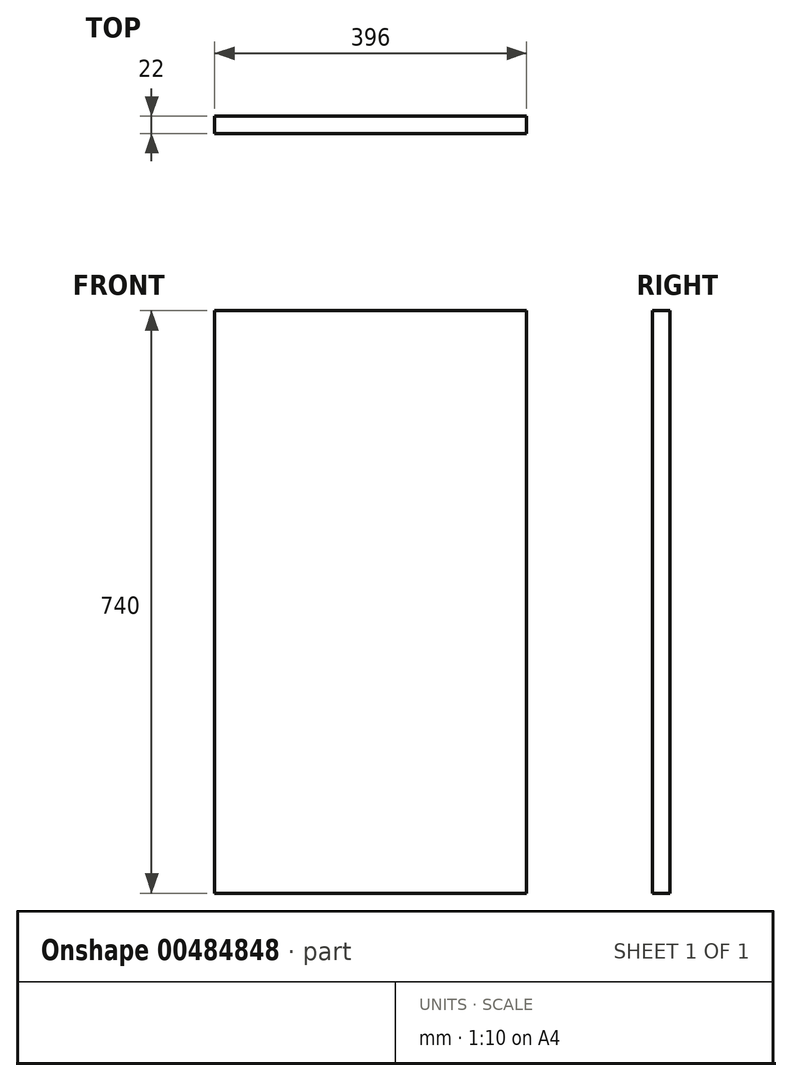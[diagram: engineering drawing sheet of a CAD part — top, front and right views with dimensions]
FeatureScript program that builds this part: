
annotation { "Feature Type Name" : "Feature", "Feature Type Description" : "" }
export const myFeature = defineFeature(function(context is Context, id is Id, definition is map)
    precondition{}
    {
        {
            var Q0;
            Q0=qCreatedBy(makeId("Front.planeOp"),FACE);
            var sketch = newSketch(context, id + "F0", { "sketchPlane" : qUnion([Q0])});
            skLineSegment(sketch, "E0.bottom", {"start": v(-244.74, 172.47) * mm, "end": v(151.26, 172.47) * mm});
            skLineSegment(sketch, "E0.top", {"start": v(-244.74, -567.53) * mm, "end": v(151.26, -567.53) * mm});
            skLineSegment(sketch, "E0.left", {"start": v(-244.74, 172.47) * mm, "end": v(-244.74, -567.53) * mm});
            skLineSegment(sketch, "E0.right", {"start": v(151.26, 172.47) * mm, "end": v(151.26, -567.53) * mm});
            skSolve(sketch);
        }
        {
            var Q0;
            Q0 = qSketchRegion(id + "F0", true);
            extrude(context, id + "F1", {"entities" : qUnion([Q0]), "depth" : 22 * mm});
        }
    });
